# Revit family: WaterConditioner_ION_SB50-SB80
name_source: partatom
category: Mechanical Equipment
revit_build: Autodesk Revit 2014 (Build: 20130308_1515(x64)
units: mm (PartAtom-declared; Revit-internal decimal feet)

## types (3) — shared parameters
Assembly Code = D2020300
Density_Water_20_ION = 998.2000 kg/m³
Equipment_Length_ION = 445 mm  [stored 1.45997 ft]
Issue_Date_ION = 01/07/15
Issue_Rev_ION = A
Manufacturer = ION Enterprises
URL = www.scalebuster.com
UnitConvert_Area = 1 m²

## per-type parameters (varying)
| type | Equipment_Dia_ION | FlangeSize | Model | UnitConvert_PressureFactor | UnitSize | Water_ConnectionDia_ION | Weight_Dry_ION |
| DN80 | 138 mm  [stored 0.452756 ft] | Flange_PN16_4Hole : DN80 | SB80 | 140252 | FlangeBody_50-80 : DN80 | 80 mm | 28.00 kg |
| DN65 | 106 mm  [stored 0.347769 ft] | Flange_PN16_4Hole : DN65 | SB65 | 432948 | FlangeBody_50-80 : DN65 | 65 mm | 16.00 kg |
| DN50 | 101 mm  [stored 0.331365 ft] | Flange_PN16_4Hole : DN50 | SB50 | 520227 | FlangeBody_50-80 : DN50 | 50 mm | 15.00 kg |

note: [stored X ft] marks values corroborated as IEEE doubles in the binary element streams (Revit-internal decimal feet)

## geometry (parser evidence)
native form markers: Sweep x6
no freeform markers — native parametric forms only
